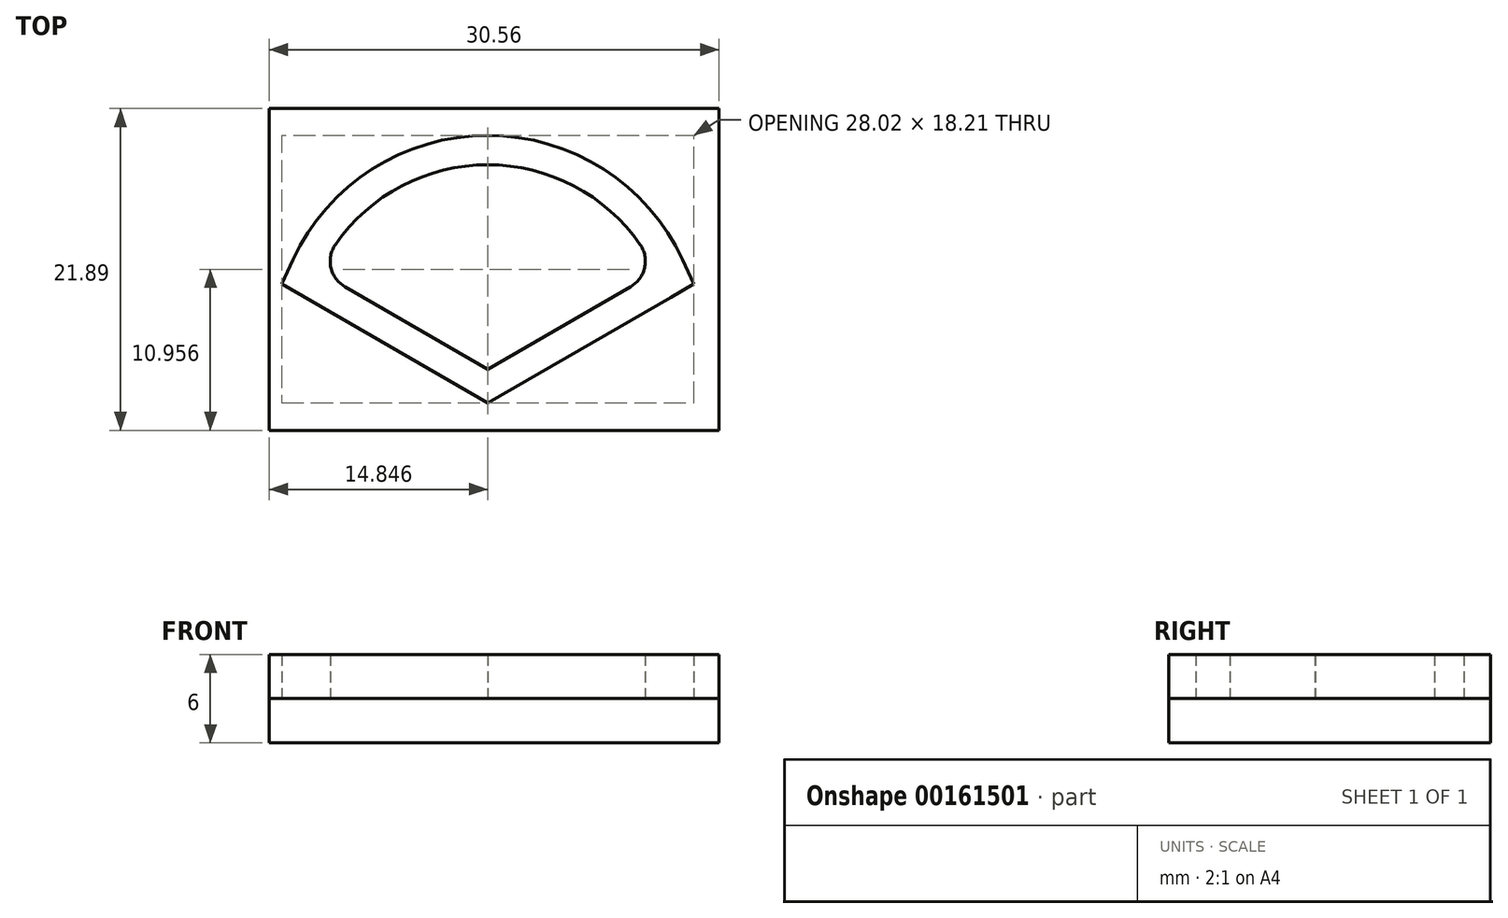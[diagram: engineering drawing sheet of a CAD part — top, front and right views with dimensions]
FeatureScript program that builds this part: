
annotation { "Feature Type Name" : "Feature", "Feature Type Description" : "" }
export const myFeature = defineFeature(function(context is Context, id is Id, definition is map)
    precondition{}
    {
        {
            var Q0;
            Q0=qCreatedBy(makeId("Top.planeOp"),FACE);
            var sketch = newSketch(context, id + "F0", { "sketchPlane" : qUnion([Q0])});
            skLineSegment(sketch, "E0", {"start": v(-28.95, 0) * mm, "end": v(-28.95, 13.2) * mm});
            skLineSegment(sketch, "E1", {"start": v(-28.95, 13.2) * mm, "end": v(-2.45, 13.2) * mm});
            skLineSegment(sketch, "E2", {"start": v(-2.45, 13.2) * mm, "end": v(-2.45, 0) * mm});
            skLineSegment(sketch, "E3", {"start": v(-45.75, 23.6) * mm, "end": v(7.18, 23.6) * mm});
            skLineSegment(sketch, "E4", {"start": v(20.73, 0) * mm, "end": v(9.3, 6.6) * mm});
            skLineSegment(sketch, "E5", {"start": v(20.73, 0) * mm, "end": v(32.16, 6.6) * mm});
            skLineSegment(sketch, "E6", {"start": v(7.74, 0) * mm, "end": v(14.43, 0) * mm, "construction": true});
            skLineSegment(sketch, "E7", {"start": v(25.51, 0) * mm, "end": v(32.41, 0) * mm, "construction": true});
            skArc(sketch, "E8", {"start": v(32.16, 6.6) * mm, "mid": v(20.73, 13.9) * mm, "end": v(9.3, 6.6) * mm});
            skLineSegment(sketch, "E9", {"start": v(-45.75, 23.6) * mm, "end": v(-45.75, 21.6) * mm});
            skLineSegment(sketch, "E10", {"start": v(-45.75, 21.6) * mm, "end": v(7.19, 21.6) * mm});
            skLineSegment(sketch, "E11", {"start": v(7.19, 21.6) * mm, "end": v(7.18, 23.6) * mm});
            skArc(sketch, "E12.0", {"start": v(33.98, 7.44) * mm, "mid": v(20.73, 15.9) * mm, "end": v(7.48, 7.44) * mm});
            skLineSegment(sketch, "E13.0", {"start": v(19.73, -1.73) * mm, "end": v(8.3, 4.87) * mm});
            skLineSegment(sketch, "E14.0", {"start": v(21.73, -1.73) * mm, "end": v(33.16, 4.87) * mm});
            skLineSegment(sketch, "E15", {"start": v(33.16, 4.87) * mm, "end": v(34.74, 5.8) * mm});
            skLineSegment(sketch, "E16", {"start": v(33.98, 7.44) * mm, "end": v(34.74, 5.8) * mm});
            skLineSegment(sketch, "E17", {"start": v(8.3, 4.87) * mm, "end": v(6.71, 5.78) * mm});
            skLineSegment(sketch, "E18", {"start": v(7.48, 7.44) * mm, "end": v(6.71, 5.78) * mm});
            skLineSegment(sketch, "E19.bottom", {"start": v(5.88, 17.73) * mm, "end": v(36.44, 17.73) * mm});
            skLineSegment(sketch, "E19.top", {"start": v(5.88, -4.16) * mm, "end": v(36.44, -4.16) * mm});
            skLineSegment(sketch, "E19.left", {"start": v(5.88, 17.73) * mm, "end": v(5.88, -4.16) * mm});
            skLineSegment(sketch, "E19.right", {"start": v(36.44, 17.73) * mm, "end": v(36.44, -4.16) * mm});
            skLineSegment(sketch, "E20", {"start": v(21.73, -1.73) * mm, "end": v(20.73, -2.3) * mm});
            skLineSegment(sketch, "E21", {"start": v(19.73, -1.73) * mm, "end": v(18.7, -1.14) * mm});
            skLineSegment(sketch, "E22", {"start": v(19.73, -1.73) * mm, "end": v(20.73, -2.3) * mm});
            skSolve(sketch);
        }
        {
            var Q0;
            Q0=makeQuery(id+"F0.imprint","IMPRINT",FACE,{"disambiguationData":[TD([[makeQuery(id+"F0.imprint","IMPRINT",EDGE,{"derivedFrom":sQuery(id+"F0.wireOp",EDGE,"E12.0")}),-1.0]])]});
            var Q1;
            Q1=makeQuery(id+"F0.imprint","IMPRINT",FACE,{"disambiguationData":[TD([[makeQuery(id+"F0.imprint","IMPRINT",EDGE,{"derivedFrom":sQuery(id+"F0.wireOp",EDGE,"E4")}),-1.0]])]});
            extrude(context, id + "F1", {"entities" : qUnion([Q0, Q1]), "depth" : 3 * mm});
        }
        {
            var Q0;
            Q0=makeQuery(id+"F1.opExtrude","CAP_FACE",FACE,{"disambiguationData":[OSD([sQuery(id+"F0.wireOp",EDGE,"E12.0"),sQuery(id+"F0.wireOp",EDGE,"E13.0"),sQuery(id+"F0.wireOp",EDGE,"E14.0"),sQuery(id+"F0.wireOp",EDGE,"E15"),sQuery(id+"F0.wireOp",EDGE,"E16"),sQuery(id+"F0.wireOp",EDGE,"E17"),sQuery(id+"F0.wireOp",EDGE,"E18"),sQuery(id+"F0.wireOp",EDGE,"E19.bottom"),sQuery(id+"F0.wireOp",EDGE,"E19.top"),sQuery(id+"F0.wireOp",EDGE,"E19.left"),sQuery(id+"F0.wireOp",EDGE,"E19.right"),sQuery(id+"F0.wireOp",EDGE,"E20"),sQuery(id+"F0.wireOp",EDGE,"E21"),sQuery(id+"F0.wireOp",EDGE,"E22")])],"isStart":true});
            var sketch = newSketch(context, id + "F2", { "sketchPlane" : qUnion([Q0])});
            skLineSegment(sketch, "E23.bottom", {"start": v(5.88, -17.73) * mm, "end": v(36.44, -17.73) * mm});
            skLineSegment(sketch, "E23.top", {"start": v(5.88, 4.16) * mm, "end": v(36.44, 4.16) * mm});
            skLineSegment(sketch, "E23.left", {"start": v(5.88, -17.73) * mm, "end": v(5.88, 4.16) * mm});
            skLineSegment(sketch, "E23.right", {"start": v(36.44, -17.73) * mm, "end": v(36.44, 4.16) * mm});
            skSolve(sketch);
        }
        {
            var Q0;
            Q0 = qSketchRegion(id + "F2", true);
            extrude(context, id + "F3", {"entities" : qUnion([Q0]), "depth" : 3 * mm});
        }
        {
            var Q0;
            Q0=makeQuery(id+"F1.opExtrude","SWEPT_EDGE",EDGE,{"disambiguationData":[OSD([sQuery(id+"F0.wireOp",EDGE,"E4"),sQuery(id+"F0.wireOp",EDGE,"E8")])]});
            fillet(context, id + "F4", {"entities" : qUnion([Q0]), "radius" : 2 * mm, "tangentPropagation" : true, "allowEdgeOverflow" : false});
        }
        {
            var Q0;
            Q0=makeQuery(id+"F1.opExtrude","SWEPT_EDGE",EDGE,{"disambiguationData":[OSD([sQuery(id+"F0.wireOp",EDGE,"E5"),sQuery(id+"F0.wireOp",EDGE,"E8")])]});
            fillet(context, id + "F5", {"entities" : qUnion([Q0]), "radius" : 2 * mm, "tangentPropagation" : true, "allowEdgeOverflow" : false});
        }
    });
